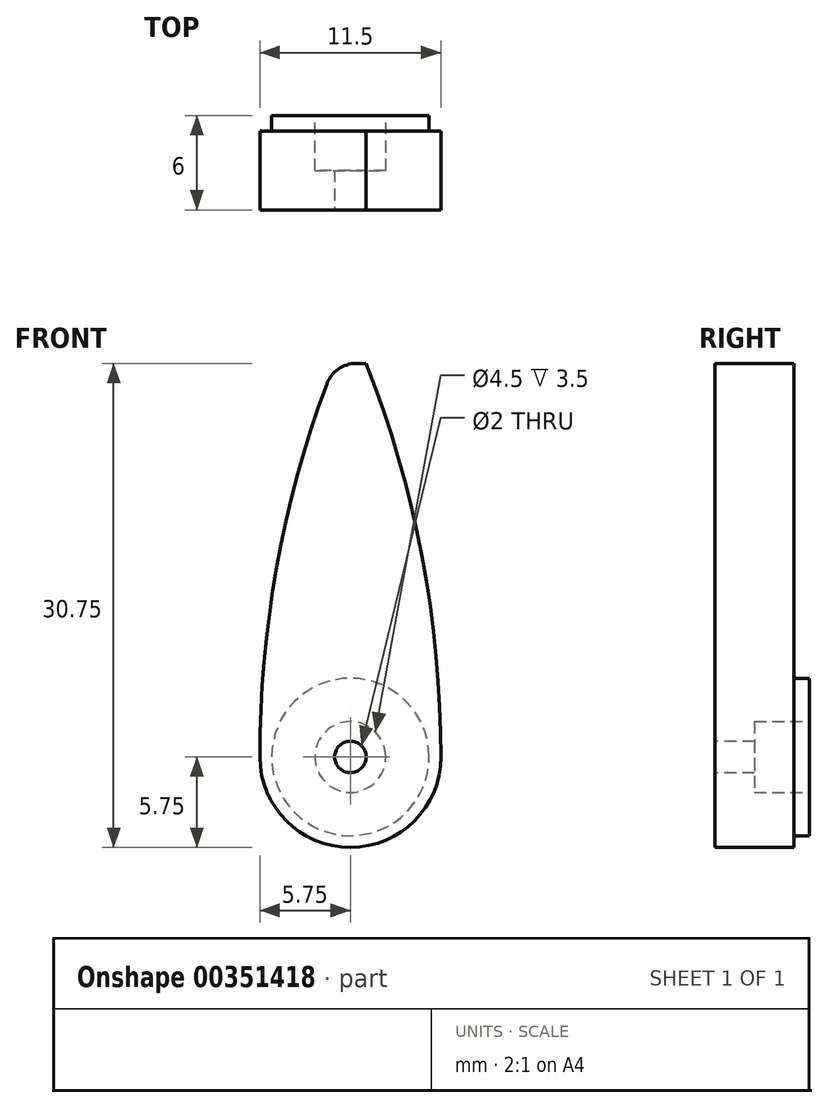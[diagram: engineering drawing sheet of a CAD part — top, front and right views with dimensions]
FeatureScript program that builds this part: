
annotation { "Feature Type Name" : "Feature", "Feature Type Description" : "" }
export const myFeature = defineFeature(function(context is Context, id is Id, definition is map)
    precondition{}
    {
        {
            var Q0;
            Q0=qCreatedBy(makeId("Front.planeOp"),FACE);
            var sketch = newSketch(context, id + "F0", { "sketchPlane" : qUnion([Q0])});
            skCircle(sketch, "E0", {"center": v(0, 0) * mm, "radius": 5 * mm});
            skSolve(sketch);
        }
        {
            var Q0;
            Q0 = qSketchRegion(id + "F0", true);
            extrude(context, id + "F1", {"entities" : qUnion([Q0]), "depth" : 1 * mm});
        }
        {
            var Q0;
            Q0=makeQuery(id+"F1.opExtrude","CAP_FACE",FACE,{"disambiguationData":[OSD([sQuery(id+"F0.wireOp",EDGE,"E0")])],"isStart":false});
            var sketch = newSketch(context, id + "F2", { "sketchPlane" : qUnion([Q0])});
            skLineSegment(sketch, "E1.bottom", {"start": v(5.75, 0) * mm, "end": v(-5.75, 0) * mm, "construction": true});
            skLineSegment(sketch, "E1.top", {"start": v(5.75, 0) * mm, "end": v(-5.75, 0) * mm, "construction": true});
            skLineSegment(sketch, "E1.left", {"start": v(5.75, 0) * mm, "end": v(5.75, 0) * mm});
            skLineSegment(sketch, "E1.right", {"start": v(-5.75, 0) * mm, "end": v(-5.75, 0) * mm});
            skPoint(sketch, "E1.middle", {"position": v(0, 0) * mm});
            skLineSegment(sketch, "E2", {"start": v(0, 0) * mm, "end": v(0, 25) * mm, "construction": true});
            skArc(sketch, "E3", {"start": v(-5.75, 0) * mm, "mid": v(0, -5.75) * mm, "end": v(5.75, 0) * mm});
            skLineSegment(sketch, "E4.bottom", {"start": v(1, 25) * mm, "end": v(-1, 25) * mm});
            skLineSegment(sketch, "E4.top", {"start": v(1, 25) * mm, "end": v(-1, 25) * mm});
            skLineSegment(sketch, "E4.left", {"start": v(1, 25) * mm, "end": v(1, 25) * mm});
            skLineSegment(sketch, "E4.right", {"start": v(-1, 25) * mm, "end": v(-1, 25) * mm});
            skPoint(sketch, "E4.middle", {"position": v(0, 25) * mm});
            skArc(sketch, "E5", {"start": v(-1, 25) * mm, "mid": v(-4.55, 12.72) * mm, "end": v(-5.75, 0) * mm});
            skArc(sketch, "E6", {"start": v(5.75, 0) * mm, "mid": v(4.55, 12.72) * mm, "end": v(1, 25) * mm});
            skSolve(sketch);
        }
        {
            var Q0;
            Q0 = qSketchRegion(id + "F2", true);
            extrude(context, id + "F3", {"entities" : qUnion([Q0]), "operationType" : NewBodyOperationType.ADD, "depth" : 5 * mm});
        }
        {
            var Q0;
            Q0=makeQuery(id+"F1.opExtrude","CAP_FACE",FACE,{"disambiguationData":[OSD([sQuery(id+"F0.wireOp",EDGE,"E0")])],"isStart":true});
            var sketch = newSketch(context, id + "F4", { "sketchPlane" : qUnion([Q0])});
            skCircle(sketch, "E7", {"center": v(0, 0) * mm, "radius": 2.25 * mm});
            skSolve(sketch);
        }
        {
            var Q0;
            Q0 = qSketchRegion(id + "F4", true);
            extrude(context, id + "F5", {"entities" : qUnion([Q0]), "operationType" : NewBodyOperationType.REMOVE, "oppositeDirection" : true, "depth" : 3.5 * mm});
        }
        {
            var Q0;
            Q0=makeQuery(id+"F3.opExtrude","CAP_FACE",FACE,{"disambiguationData":[OSD([sQuery(id+"F2.wireOp",EDGE,"E3"),sQuery(id+"F2.wireOp",EDGE,"E4.top"),sQuery(id+"F2.wireOp",EDGE,"E5"),sQuery(id+"F2.wireOp",EDGE,"E6")])],"isStart":false});
            var sketch = newSketch(context, id + "F6", { "sketchPlane" : qUnion([Q0])});
            skCircle(sketch, "E8", {"center": v(0, 0) * mm, "radius": 1 * mm});
            skSolve(sketch);
        }
        {
            var Q0;
            Q0 = qSketchRegion(id + "F6", true);
            extrude(context, id + "F7", {"entities" : qUnion([Q0]), "operationType" : NewBodyOperationType.REMOVE, "oppositeDirection" : true, "depth" : 25 * mm});
        }
        {
            var Q0;
            Q0=makeQuery(id+"F3.opExtrude","SWEPT_EDGE",EDGE,{"disambiguationData":[OSD([sQuery(id+"F2.wireOp",EDGE,"E4.top"),sQuery(id+"F2.wireOp",EDGE,"E5")])]});
            fillet(context, id + "F8", {"entities" : qUnion([Q0]), "radius" : 2 * mm, "tangentPropagation" : true, "allowEdgeOverflow" : false});
        }
    });
